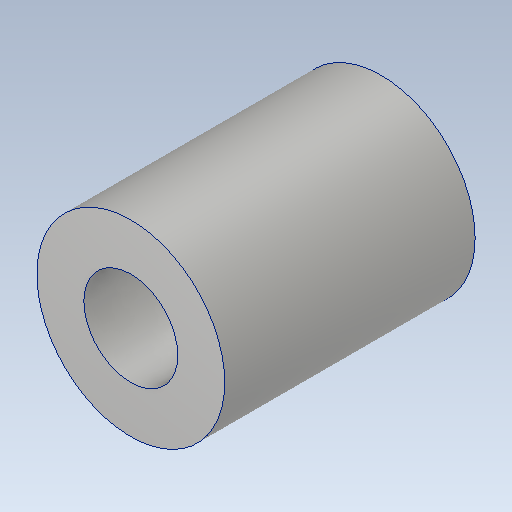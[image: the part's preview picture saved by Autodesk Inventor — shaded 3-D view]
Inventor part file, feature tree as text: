
AUTODESK INVENTOR PART (.ipt)
format: ipt  version: 2020.2 (Build 242310000, 310)  size: 114,176 bytes
history: native  units: mm
features: other x1, extrude x1, sketch x1
ambient origin geometry x8: Origin, YZ Plane, XZ Plane, XY Plane, X Axis, Y Axis, Z Axis, Center Point
bodies: Body1 (feature_tree)
feature tree (3):
  other  "ソリッド1"
  extrude  "押し出し1"  Depth=6.0mm
  sketch  "スケッチ1"
